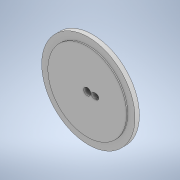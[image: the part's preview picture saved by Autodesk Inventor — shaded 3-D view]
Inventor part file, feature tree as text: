
AUTODESK INVENTOR PART (.ipt)
format: ipt  version: 2021 (Build 250183000, 183)  size: 148,992 bytes
history: native  units: mm
features: sketch x6, extrude x4, plane x1, hole x1, other x1
ambient origin geometry x8: Origin, YZ Plane, XZ Plane, XY Plane, X Axis, Y Axis, Z Axis, Center Point
bodies: Solid1 (feature_tree)
feature tree (13):
  extrude  "Extrusion1"  Depth=8.0mm TaperAngle=0.0deg
  extrude  "Extrusion2"  Depth=2.0mm TaperAngle=0.0deg
  extrude  "Extrusion3"  TaperAngle=0.0deg  [1 undecoded]
  sketch  "Sketch4"  dims[d9=45.0mm d10=3.490659mm]
  plane  "Work Plane1"
  extrude  "Extrusion4"  Depth=3.490659mm
  hole  "Hole1"  [1 undecoded]
  sketch  "Sketch1"  dims[d0=170.0mm d1=8.0mm d2=0.0mm]
  sketch  "Sketch2"  dims[d3=143.5mm d4=2.0mm d5=0.0mm]
  sketch  "Sketch3"  dims[d6=13.0mm d7=0.0mm d8=0.0mm]
  other  "Work Point1"
  sketch  "Sketch5"  dims[d12=10.0mm d13=2.819078mm]
  sketch  "Sketch10"  dims[d14=0.0mm d15=0.0mm d37=2.0mm d50=30.0mm d53=2.459mm d54=6.0mm d55=4.0mm d56=2.0mm d57=90.0deg d58=6.0mm d59=20.594885mm d60=11.65mm d61=1.0mm]
note: 2 required parameter values undecoded (feature->parameter linkage not recoverable at this tier; creation-order binding heuristic only, values carry confidence <= 0.55)
